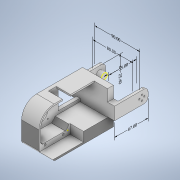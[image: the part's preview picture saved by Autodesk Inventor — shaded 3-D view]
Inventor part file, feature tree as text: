
AUTODESK INVENTOR PART (.ipt)
format: ipt  version: 2022 (Build 260153000, 153)  size: 1,463,808 bytes
history: native  units: mm
features: sketch x35, extrude x33, other x9, fillet x3, plane x1
ambient origin geometry x8: Origin, YZ Plane, XZ Plane, XY Plane, X Axis, Y Axis, Z Axis, Center Point
bodies: Solid1 (feature_tree)
feature tree (81):
  other  "Assembly2.iam"
  other  "96Gears_Stage_1_modified.ipt:1"
  other  "96Gears_Stage_2_modified.ipt:1"
  other  "Annotations"
  extrude  "Extrusion3"  Depth=10.0mm
  extrude  "Extrusion5"  Depth=18.0mm TaperAngle=0.0deg
  extrude  "Extrusion6"  Depth=6.0mm TaperAngle=0.0deg
  extrude  "Extrusion7"  Depth=10.0mm TaperAngle=0.0deg
  extrude  "Extrusion8"  Depth=4.1mm
  extrude  "Extrusion9"  Depth=7.0mm
  extrude  "Extrusion10"  Depth=50.0mm TaperAngle=0.0deg
  extrude  "Extrusion11"  Depth=50.0mm TaperAngle=0.0deg
  extrude  "Extrusion12"  Depth=3.0mm TaperAngle=0.0deg
  extrude  "Extrusion13"  Depth=3.0mm TaperAngle=0.0deg
  extrude  "Extrusion14"  Depth=9.0mm TaperAngle=0.0deg
  extrude  "Extrusion15"  Depth=9.0mm TaperAngle=0.0deg
  extrude  "Extrusion16"  Depth=30.0mm
  fillet  "Fillet1"  Radius=5.0mm
  extrude  "Extrusion17"  Depth=10.0mm TaperAngle=0.0deg
  extrude  "Extrusion18"  Depth=10.0mm TaperAngle=0.0deg
  extrude  "Extrusion19"  Depth=13.0mm TaperAngle=0.0deg
  extrude  "Extrusion20"  Depth=13.0mm TaperAngle=0.0deg
  extrude  "Extrusion21"  Depth=24.0mm
  extrude  "Extrusion22"  Depth=5.0mm
  extrude  "Extrusion23"  Depth=55.0mm TaperAngle=0.0deg
  extrude  "Extrusion24"  Depth=55.0mm TaperAngle=0.0deg
  extrude  "Extrusion25"  Depth=10.0mm
  fillet  "Fillet2"  Radius=5.0mm
  extrude  "Extrusion26"  Depth=8.0mm TaperAngle=0.0deg
  fillet  "Fillet3"  Radius=12.0mm
  extrude  "Extrusion27"  Depth=10.0mm TaperAngle=0.0deg
  extrude  "Extrusion31"  Depth=16.0mm
  extrude  "Extrusion32"  Depth=10.0mm TaperAngle=0.0deg
  extrude  "Extrusion33"  Depth=10.0mm TaperAngle=0.0deg
  extrude  "Extrusion34"  Depth=10.0mm TaperAngle=0.0deg
  sketch  "Sketch37"  dims[d103=2.161817mm d104=5.384355mm d105=80.0mm d106=6.851437mm d107=7.526531mm d108=90.0mm d109=2.261432mm d110=4.924128mm d111=55.0mm d112=3.454791mm d113=3.105941mm d114=67.0mm d115=9.287367mm d116=9.070993mm d117=25.4mm d154=0.5mm]
  plane  "Work Plane3"
  extrude  "Extrusion35"  TaperAngle=0.0deg  [1 undecoded]
  extrude  "Extrusion36"  Depth=0.5mm
  extrude  "Extrusion37"  [1 undecoded]
  extrude  "Extrusion38"  [1 undecoded]
  extrude  "Extrusion39"  [1 undecoded]
  sketch  "Sketch5"  dims[d7=6.0mm d8=18.0mm d9=0.0mm]
  sketch  "Sketch4"  dims[d0=10.0mm d6=3.0mm]
  sketch  "Sketch7"  dims[d17=32.25mm d18=6.0mm d19=0.0mm]
  sketch  "Sketch8"  dims[d20=10.0mm d21=10.0mm d22=0.0mm]
  sketch  "Sketch9"  dims[d24=4.1mm d25=4.1mm]
  sketch  "Sketch10"  dims[d26=10.0mm d27=0.0mm d28=7.0mm]
  sketch  "Sketch11"  dims[d29=0.0mm d30=0.0mm d31=50.0mm d32=0.0mm]
  sketch  "Sketch12"  dims[d33=3.0mm d34=50.0mm d35=0.0mm]
  sketch  "Sketch13"  dims[d38=3.0mm d39=3.0mm d40=0.0mm]
  sketch  "Sketch14"  dims[d41=23.0mm d42=3.0mm d43=0.0mm]
  sketch  "Sketch15"  dims[d44=3.0mm d45=0.0mm d46=9.0mm d47=0.0mm]
  sketch  "Sketch16"  dims[d49=33.25mm d50=9.0mm d51=0.0mm]
  sketch  "Sketch17"  dims[d52=2.0mm d53=0.0mm d54=30.0mm d55=5.0mm]
  sketch  "Sketch18"  dims[d57=5.0mm d58=10.0mm d59=0.0mm]
  sketch  "Sketch19"  dims[d60=3.0mm d61=10.0mm d62=0.0mm]
  sketch  "Sketch20"  dims[d63=2.0mm d64=0.0mm d65=13.0mm d66=0.0mm]
  sketch  "Sketch21"  dims[d67=32.25mm d68=13.0mm d69=0.0mm]
  sketch  "Sketch22"  dims[d76=14.0mm d77=24.0mm]
  sketch  "Sketch23"  dims[d78=12.0mm d79=0.0mm d80=5.0mm]
  sketch  "Sketch24"  dims[d81=5.0mm d82=55.0mm d83=0.0mm]
  sketch  "Sketch25"  dims[d92=40.0mm d94=360.0deg d96=55.0mm d97=0.0mm]
  sketch  "Sketch26"  dims[d101=10.0mm d102=0.0mm d118=5.75mm d119=5.0mm d120=0.0mm]
  sketch  "Sketch27"  dims[d121=8.0mm d125=8.0mm d126=0.0mm d144=12.0mm d145=0.0mm]
  sketch  "Sketch28"  dims[d146=10.0mm d147=0.0mm d148=10.0mm d149=0.0mm]
  sketch  "Sketch29"  dims[d150=8.0mm d151=16.0mm]
  sketch  "Sketch33"  dims[d152=10.0mm d153=0.0mm d156=4.2mm d157=0.0mm]
  sketch  "Sketch34"  dims[d158=10.0mm d159=0.0mm d160=10.0mm d161=0.0mm]
  sketch  "Sketch35"  dims[d163=30.75mm d164=10.0mm d165=0.0mm]
  sketch  "Sketch36"  dims[d170=2.5mm d171=0.0mm d172=0.0mm]
  sketch  "Sketch38"  dims[d155=0.872665mm]
  sketch  "Sketch39"
  sketch  "Sketch40"
  sketch  "Sketch42"
  sketch  "Sketch43"
  other  "Linear Dimension 1"
  other  "Linear Dimension 2"
  other  "Linear Dimension 3"
  other  "Linear Dimension 4"
  other  "Linear Dimension 5"
note: 4 required parameter values undecoded (feature->parameter linkage not recoverable at this tier; creation-order binding heuristic only, values carry confidence <= 0.55)
